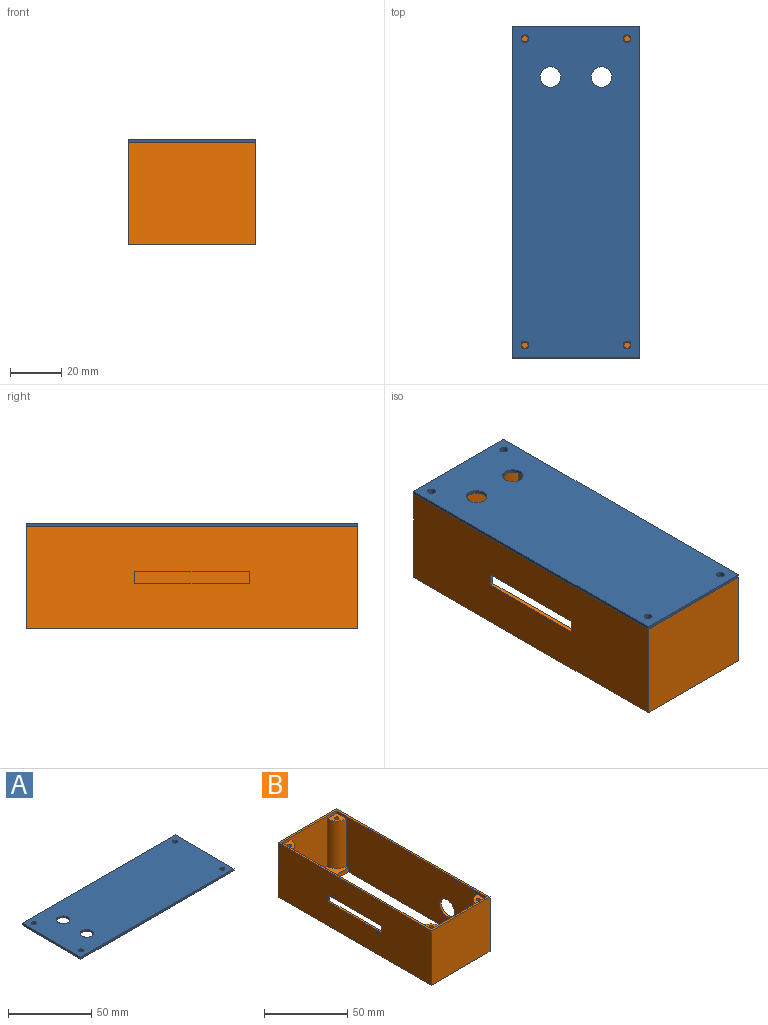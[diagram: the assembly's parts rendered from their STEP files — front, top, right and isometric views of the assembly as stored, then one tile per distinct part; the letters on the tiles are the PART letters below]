
ASSEMBLY  parts=2 mates=1
PART A: 26 faces, bbox 130x50x3.2 mm
  f0: plane 130x50mm, normal (0,0,1), area 6371.2mm2, adj f8,f9,f10,f11,f16,f17,f22,f23
  f1: plane 126.5x46.5mm, normal (0,0,-1), area 441.4mm2, adj f2,f3,f5,f6,f12,f13,f14,f15
  f2: plane 111.2x2mm, normal (0,-1,0), area 222.4mm2, adj f1,f4,f20,f21
  f3: plane 31.2x2mm, normal (-1,0,0), area 62.4mm2, adj f1,f4,f19,f21
  f4: plane 124.5x44.5mm, normal (0,0,-1), area 5312.1mm2, adj f2,f3,f5,f6,f16,f17,f18,f19
  f5: plane 31.2x2mm, normal (1,0,0), area 62.4mm2, adj f1,f4,f18,f20
  f6: plane 111.2x2mm, normal (0,1,0), area 222.4mm2, adj f1,f4,f18,f19
  f7: plane 130x50mm, normal (0,0,-1), area 617.8mm2, adj f8,f9,f10,f11,f12,f13,f14,f15
  f8: plane 130x1.2mm, normal (0,-1,0), area 156mm2, adj f0,f7,f9,f11
  f9: plane 50x1.2mm, normal (1,0,0), area 60mm2, adj f0,f7,f8,f10
  f10: plane 130x1.2mm, normal (0,1,0), area 156mm2, adj f0,f7,f9,f11
  f11: plane 50x1.2mm, normal (-1,0,0), area 60mm2, adj f0,f7,f8,f10
  f12: plane 46.5x2mm, normal (-1,0,0), area 93mm2, adj f1,f7,f13,f15
  f13: plane 126.5x2mm, normal (0,-1,0), area 253mm2, adj f1,f7,f12,f14
  f14: plane 46.5x2mm, normal (1,0,0), area 93mm2, adj f1,f7,f13,f15
  f15: plane 126.5x2mm, normal (0,1,0), area 253mm2, adj f1,f7,f12,f14
  f16: cylinder r=4mm len=8mm, axis (0,0,1), area 30.2mm2, adj f0,f4
  f17: cylinder r=4mm len=8mm, axis (0,0,1), area 30.2mm2, adj f0,f4
  f18: cylinder r=8mm len=6.65mm, axis (0,0,1), area 20.1mm2, adj f1,f4,f5,f6
  f19: cylinder r=8mm len=6.65mm, axis (0,0,1), area 20.1mm2, adj f1,f3,f4,f6
  f20: cylinder r=8mm len=6.65mm, axis (0,0,1), area 20.1mm2, adj f1,f2,f4,f5
  f21: cylinder r=8mm len=6.65mm, axis (0,0,1), area 20.1mm2, adj f1,f2,f3,f4
  f22: cylinder r=1.5mm len=3.2mm, axis (0,0,-1), area 30.2mm2, adj f0,f1
  f23: cylinder r=1.5mm len=3.2mm, axis (0,0,-1), area 30.2mm2, adj f0,f1
  f24: cylinder r=1.5mm len=3.2mm, axis (0,0,-1), area 30.2mm2, adj f0,f1
  f25: cylinder r=1.5mm len=3.2mm, axis (0,0,-1), area 30.2mm2, adj f0,f1
PART B: 37 faces, bbox 50x130x40 mm
  f0: plane 127x40mm, normal (1,0,0), area 4235mm2, adj f2,f3,f4,f5,f6,f11,f12,f13
  f1: plane 130x40mm, normal (-1,0,0), area 4975mm2, adj f2,f6,f7,f9,f32,f33,f34,f35
  f2: plane 130x50mm, normal (0,0,-1), area 1445.9mm2, adj f0,f1,f7,f8,f9,f10,f12,f13
  f3: plane 47x10mm, normal (0,0,1), area 356.9mm2, adj f0,f10,f11,f13,f22,f24,f26
  f4: plane 47x37mm, normal (0,1,0), area 1179mm2, adj f0,f5,f6,f10,f14,f15,f16,f17
  f5: plane 47x10mm, normal (0,0,1), area 356.9mm2, adj f0,f4,f10,f12,f14,f16,f27
  f6: plane 130x50mm, normal (0,0,1), area 531mm2, adj f0,f1,f4,f7,f8,f9,f10,f11
  f7: plane 50x40mm, normal (0,-1,0), area 2000mm2, adj f1,f2,f6,f8
  f8: plane 130x40mm, normal (1,0,0), area 5077.3mm2, adj f2,f6,f7,f9,f36
  f9: plane 50x40mm, normal (0,1,0), area 2000mm2, adj f1,f2,f6,f8
  f10: plane 127x40mm, normal (-1,0,0), area 4337.3mm2, adj f2,f3,f4,f5,f6,f11,f12,f13
  f11: plane 47x37mm, normal (0,-1,0), area 1179mm2, adj f0,f3,f6,f10,f22,f23,f24,f25
  f12: plane 47x3mm, normal (0,1,0), area 141mm2, adj f0,f2,f5,f10
  f13: plane 47x3mm, normal (0,-1,0), area 141mm2, adj f0,f2,f3,f10
  f14: cylinder r=8mm len=35mm, axis (0,0,-1), area 439.8mm2, adj f4,f5,f10,f15
  f15: plane 8x8mm, normal (0,0,1), area 45.4mm2, adj f4,f10,f14,f20
  f16: cylinder r=8mm len=35mm, axis (0,0,-1), area 439.8mm2, adj f0,f4,f5,f17
  f17: plane 8x8mm, normal (0,0,1), area 45.4mm2, adj f0,f4,f16,f18
  f18: cylinder r=1.25mm len=30mm, axis (0,0,1), area 235.6mm2, adj f17,f19
  f19: plane 2.5x2.5mm, normal (0,0,1), area 4.9mm2, adj f18
  f20: cylinder r=1.25mm len=30mm, axis (0,0,1), area 235.6mm2, adj f15,f21
  f21: plane 2.5x2.5mm, normal (0,0,1), area 4.9mm2, adj f20
  f22: cylinder r=8mm len=35mm, axis (0,0,-1), area 439.8mm2, adj f0,f3,f11,f23
  f23: plane 8x8mm, normal (0,0,1), area 45.4mm2, adj f0,f11,f22,f30
  f24: cylinder r=8mm len=35mm, axis (0,0,-1), area 439.8mm2, adj f3,f10,f11,f25
  f25: plane 8x8mm, normal (0,0,1), area 45.4mm2, adj f10,f11,f24,f28
  f26: cylinder r=2mm len=4mm, axis (0,0,1), area 37.7mm2, adj f2,f3
  f27: cylinder r=2mm len=4mm, axis (0,0,1), area 37.7mm2, adj f2,f5
  f28: cylinder r=1.25mm len=30mm, axis (0,0,1), area 235.6mm2, adj f25,f29
  f29: plane 2.5x2.5mm, normal (0,0,1), area 4.9mm2, adj f28
  f30: cylinder r=1.25mm len=30mm, axis (0,0,1), area 235.6mm2, adj f23,f31
  f31: plane 2.5x2.5mm, normal (0,0,1), area 4.9mm2, adj f30
  f32: plane 5x1.5mm, normal (0,-1,0), area 7.5mm2, adj f0,f1,f33,f35
  f33: plane 45x1.5mm, normal (0,0,1), area 67.5mm2, adj f0,f1,f32,f34
  f34: plane 5x1.5mm, normal (0,1,0), area 7.5mm2, adj f0,f1,f33,f35
  f35: plane 45x1.5mm, normal (0,0,-1), area 67.5mm2, adj f0,f1,f32,f34
  f36: cylinder r=6.25mm len=12.5mm, axis (1,0,0), area 58.9mm2, adj f8,f10
PLACE A rot(axis=(0,0,-1),90deg) t=(70.4,8.43,-5.53)mm
PLACE B t=(70.4,8.43,-46.73)mm
MATE fastened A.f23 <-> B.f30  axis (0,0,-1) through (50.4,68.43,-8.73)mm
